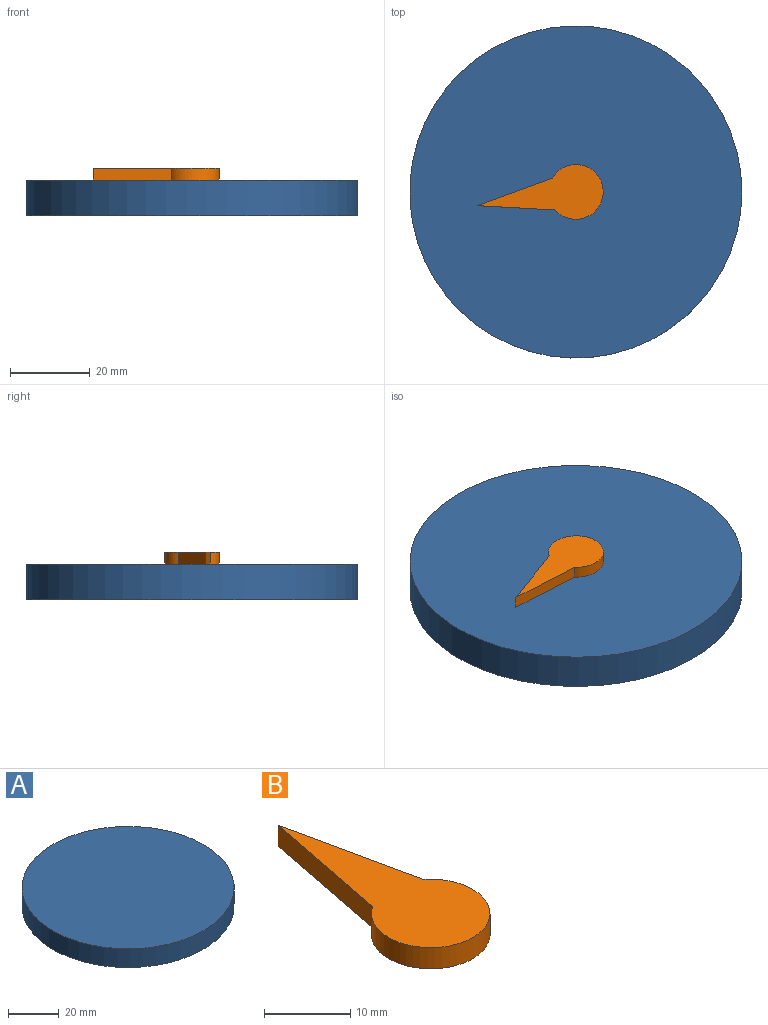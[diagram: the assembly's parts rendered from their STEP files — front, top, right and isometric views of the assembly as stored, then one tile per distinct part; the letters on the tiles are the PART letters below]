
ASSEMBLY  parts=2 mates=1
PART A: 3 faces, bbox 83.5x83.5x9 mm
  f0: cylinder r=41.75mm len=83.5mm, axis (0,0,-1), area 2360.9mm2, adj f1,f2
  f1: plane 83.5x83.5mm, normal (0,0,1), area 5475.8mm2, adj f0
  f2: plane 83.5x83.5mm, normal (0,0,-1), area 5475.8mm2, adj f0
PART B: 5 faces, bbox 13.8x31.9x3 mm
  f0: cylinder r=6.88mm len=13.75mm, axis (0,0,-1), area 103.7mm2, adj f1,f2,f3,f4
  f1: plane 19.68x4.27mm, normal (0.98,0.21,0), area 60.4mm2, adj f0,f2,f3,f4
  f2: plane 19.33x3.79mm, normal (-0.98,0.19,0), area 59.1mm2, adj f0,f1,f3,f4
  f3: plane 31.94x13.75mm, normal (0,0,1), area 219.9mm2, adj f0,f1,f2
  f4: plane 31.94x13.75mm, normal (0,0,-1), area 219.9mm2, adj f0,f1,f2
PLACE A at identity fixed
PLACE B rot(axis=(0,0,1),97.9deg) t=(0,0,0)mm
MATE revolute A.f0 <-> B.f0  axis (0,0,1) through (0,0,9)mm
